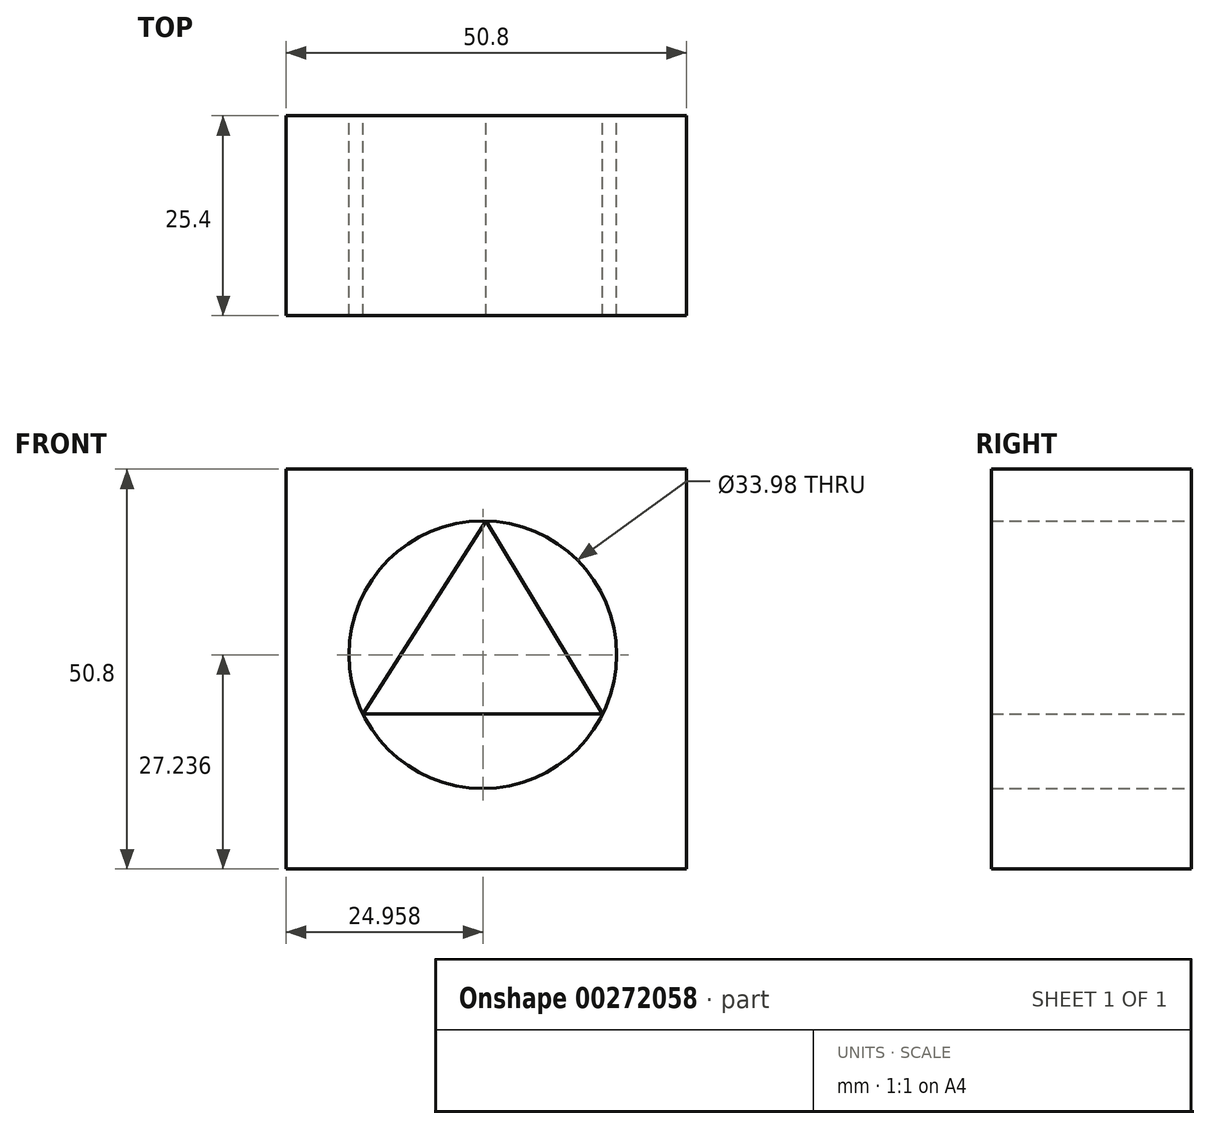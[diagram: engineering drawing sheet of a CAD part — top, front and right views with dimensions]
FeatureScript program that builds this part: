
annotation { "Feature Type Name" : "Feature", "Feature Type Description" : "" }
export const myFeature = defineFeature(function(context is Context, id is Id, definition is map)
    precondition{}
    {
        {
            var Q0;
            Q0=qCreatedBy(makeId("Front.planeOp"),FACE);
            var sketch = newSketch(context, id + "F0", { "sketchPlane" : qUnion([Q0])});
            skLineSegment(sketch, "E0.bottom", {"start": v(-42.9, 31.1) * mm, "end": v(7.9, 31.1) * mm});
            skLineSegment(sketch, "E0.top", {"start": v(-42.9, -19.7) * mm, "end": v(7.9, -19.7) * mm});
            skLineSegment(sketch, "E0.left", {"start": v(-42.9, 31.1) * mm, "end": v(-42.9, -19.7) * mm});
            skLineSegment(sketch, "E0.right", {"start": v(7.9, 31.1) * mm, "end": v(7.9, -19.7) * mm});
            skCircle(sketch, "E1", {"center": v(-17.95, 7.54) * mm, "radius": 17 * mm});
            skLineSegment(sketch, "E2", {"start": v(-33.18, 0) * mm, "end": v(-17.51, 24.52) * mm});
            skLineSegment(sketch, "E3", {"start": v(-17.51, 24.52) * mm, "end": v(-2.72, 0) * mm});
            skLineSegment(sketch, "E4", {"start": v(-2.72, 0) * mm, "end": v(-33.18, 0) * mm});
            skSolve(sketch);
        }
        {
            var Q0;
            Q0=makeQuery(id+"F0.imprint","IMPRINT",FACE,{"disambiguationData":[TD([[makeQuery(id+"F0.imprint","IMPRINT",EDGE,{"derivedFrom":sQuery(id+"F0.wireOp",EDGE,"E0.bottom")}),-1.0]])]});
            extrude(context, id + "F1", {"entities" : qUnion([Q0]), "depth" : 25.4 * mm});
        }
        {
            var Q0;
            Q0=makeQuery(id+"F0.imprint","IMPRINT",FACE,{"disambiguationData":[TD([[makeQuery(id+"F0.imprint","IMPRINT",EDGE,{"derivedFrom":sQuery(id+"F0.wireOp",EDGE,"E2")}),-1.0]])]});
            extrude(context, id + "F2", {"entities" : qUnion([Q0]), "depth" : 25.4 * mm});
        }
    });
